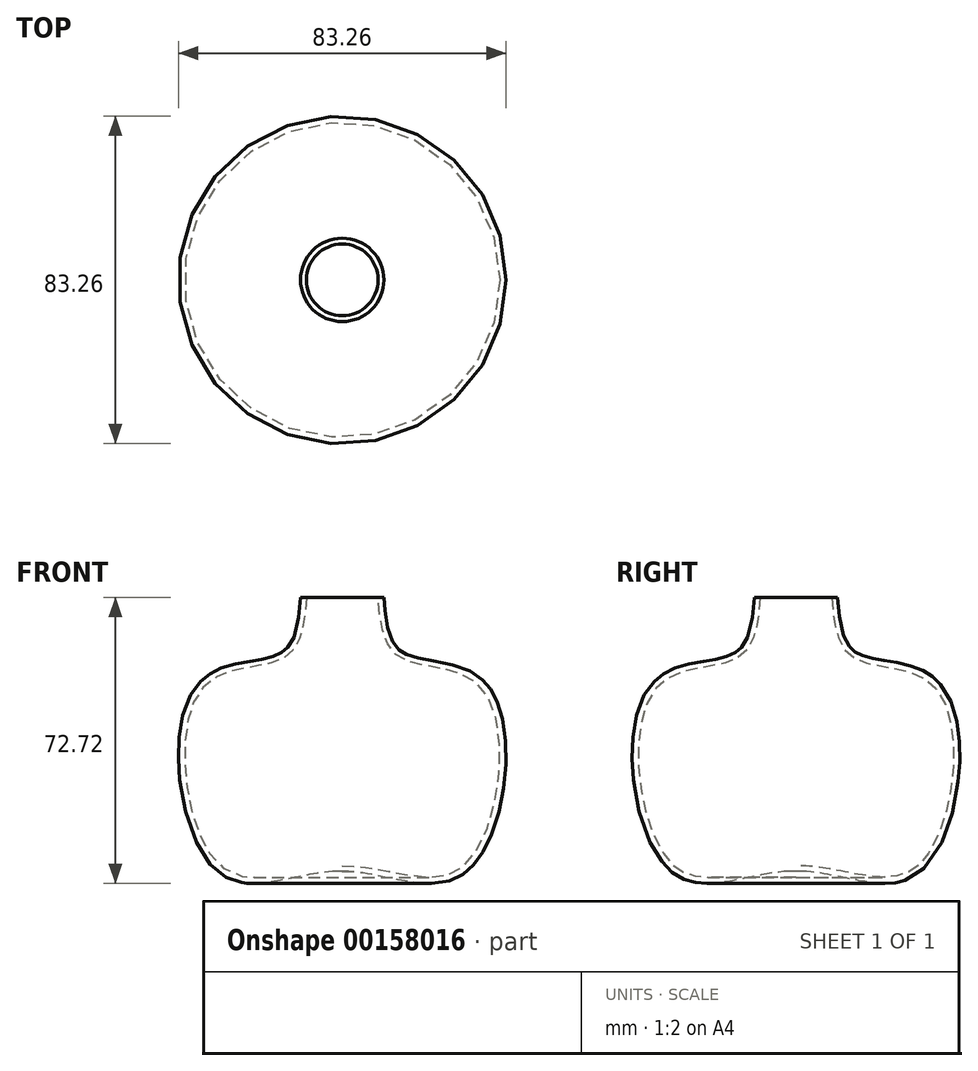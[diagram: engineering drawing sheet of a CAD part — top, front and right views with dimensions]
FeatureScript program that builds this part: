
annotation { "Feature Type Name" : "Feature", "Feature Type Description" : "" }
export const myFeature = defineFeature(function(context is Context, id is Id, definition is map)
    precondition{}
    {
        {
            var Q0;
            Q0=qCreatedBy(makeId("Front.planeOp"),FACE);
            var sketch = newSketch(context, id + "F0", { "sketchPlane" : qUnion([Q0])});
            skFitSpline(sketch, "E0", {"points": [v(0, 0) * mm, v(31.03, 0) * mm, v(36.01, 44.52) * mm, v(14.64, 52.83) * mm, v(9.1, 68.07) * mm], "startDerivative": vector(139.17, 0) * mm, "endDerivative": vector(-7.92, 97.06) * mm});
            skLineSegment(sketch, "E1", {"start": v(0, 43.53) * mm, "end": v(0, 26.12) * mm});
            skFitSpline(sketch, "E2.0", {"points": [v(0, -1.5) * mm, v(2.77, -1.5) * mm, v(6.91, -2.03) * mm, v(12.3, -3.08) * mm, v(16.22, -3.84) * mm, v(20.04, -4.39) * mm, v(23.74, -4.5) * mm, v(26.72, -4.02) * mm, v(29, -3.16) * mm, v(30.63, -2.25) * mm, v(32.17, -1.06) * mm, v(33.58, 0.42) * mm, v(34.87, 2.12) * mm, v(36.43, 4.67) * mm, v(38.1, 8.3) * mm, v(39.68, 13.22) * mm, v(40.8, 18.5) * mm, v(41.46, 23.92) * mm, v(41.62, 29.32) * mm, v(41.24, 34.48) * mm, v(40.44, 38.44) * mm, v(39.49, 41.31) * mm, v(38.6, 43.3) * mm, v(37.7, 44.78) * mm, v(36.88, 45.86) * mm, v(36, 46.84) * mm, v(34.8, 47.9) * mm, v(32.73, 49.3) * mm, v(29.94, 50.5) * mm, v(26.48, 51.4) * mm, v(23.09, 52) * mm, v(20.45, 52.45) * mm, v(18.55, 52.88) * mm, v(17.26, 53.26) * mm, v(16.33, 53.63) * mm, v(15.67, 53.96) * mm, v(15.07, 54.32) * mm, v(14.41, 54.84) * mm, v(13.72, 55.58) * mm, v(13.12, 56.43) * mm, v(12.43, 57.73) * mm, v(11.75, 59.64) * mm, v(11.2, 62.28) * mm, v(10.85, 65.17) * mm, v(10.68, 67.18) * mm, v(10.6, 68.19) * mm]});
            skLineSegment(sketch, "E3", {"start": v(9.1, 68.07) * mm, "end": v(10.6, 68.19) * mm});
            skLineSegment(sketch, "E4", {"start": v(0, 0) * mm, "end": v(0, -1.5) * mm});
            skSolve(sketch);
        }
        {
            var Q0;
            Q0=makeQuery(id+"F0.imprint","IMPRINT",FACE,{"disambiguationData":[TD([[makeQuery(id+"F0.imprint","IMPRINT",EDGE,{"derivedFrom":sQuery(id+"F0.wireOp",EDGE,"E0")}),-1.0]])]});
            var Q1;
            Q1=sQuery(id+"F0.wireOp",EDGE,"E1");
            revolve(context, id + "F1", {"entities" : qUnion([Q0]), "axis" : qUnion([Q1]), "revolveType" : RevolveType.FULL});
        }
    });
